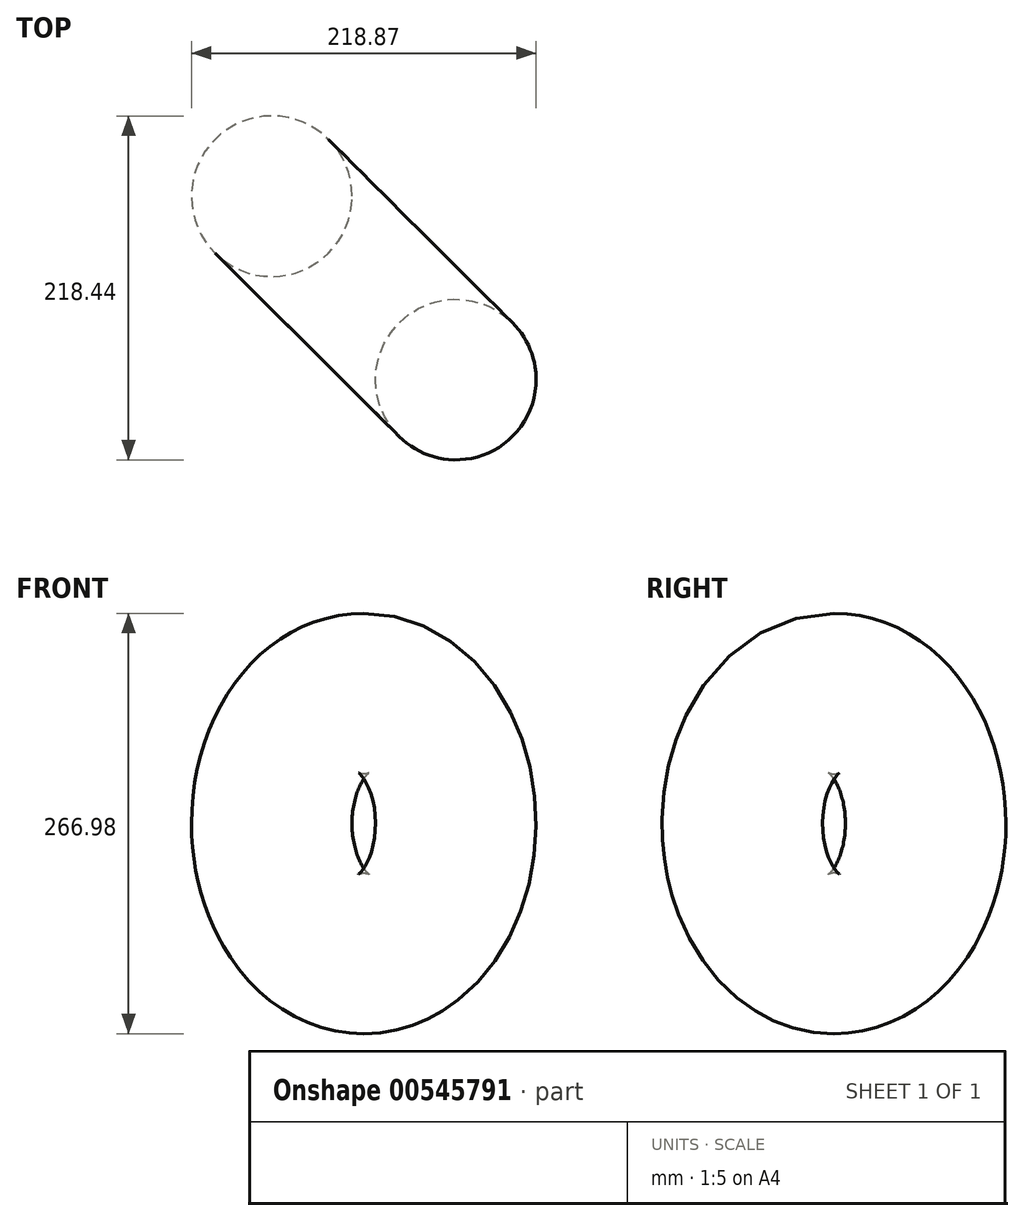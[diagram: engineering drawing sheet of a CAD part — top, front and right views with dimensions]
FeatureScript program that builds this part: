
annotation { "Feature Type Name" : "Feature", "Feature Type Description" : "" }
export const myFeature = defineFeature(function(context is Context, id is Id, definition is map)
    precondition{}
    {
        {
            var Q0;
            Q0=qCreatedBy(makeId("Top.planeOp"),FACE);
            var sketch = newSketch(context, id + "F0", { "sketchPlane" : qUnion([Q0])});
            skCircle(sketch, "E0", {"center": v(-60.99, 54.83) * mm, "radius": 51 * mm});
            skLineSegment(sketch, "E1", {"start": v(75.81, 75.25) * mm, "end": v(-74.97, -76.1) * mm});
            skSolve(sketch);
        }
        {
            var Q0;
            Q0=makeQuery(id+"F0.imprint","IMPRINT",FACE,{"disambiguationData":[TD([[makeQuery(id+"F0.imprint","IMPRINT",EDGE,{"derivedFrom":sQuery(id+"F0.wireOp",EDGE,"E0")}),1.0]])]});
            var Q1;
            Q1=sQuery(id+"F0.wireOp",EDGE,"E1");
            revolve(context, id + "F1", {"entities" : qUnion([Q0]), "axis" : qUnion([Q1]), "revolveType" : RevolveType.FULL});
        }
    });
